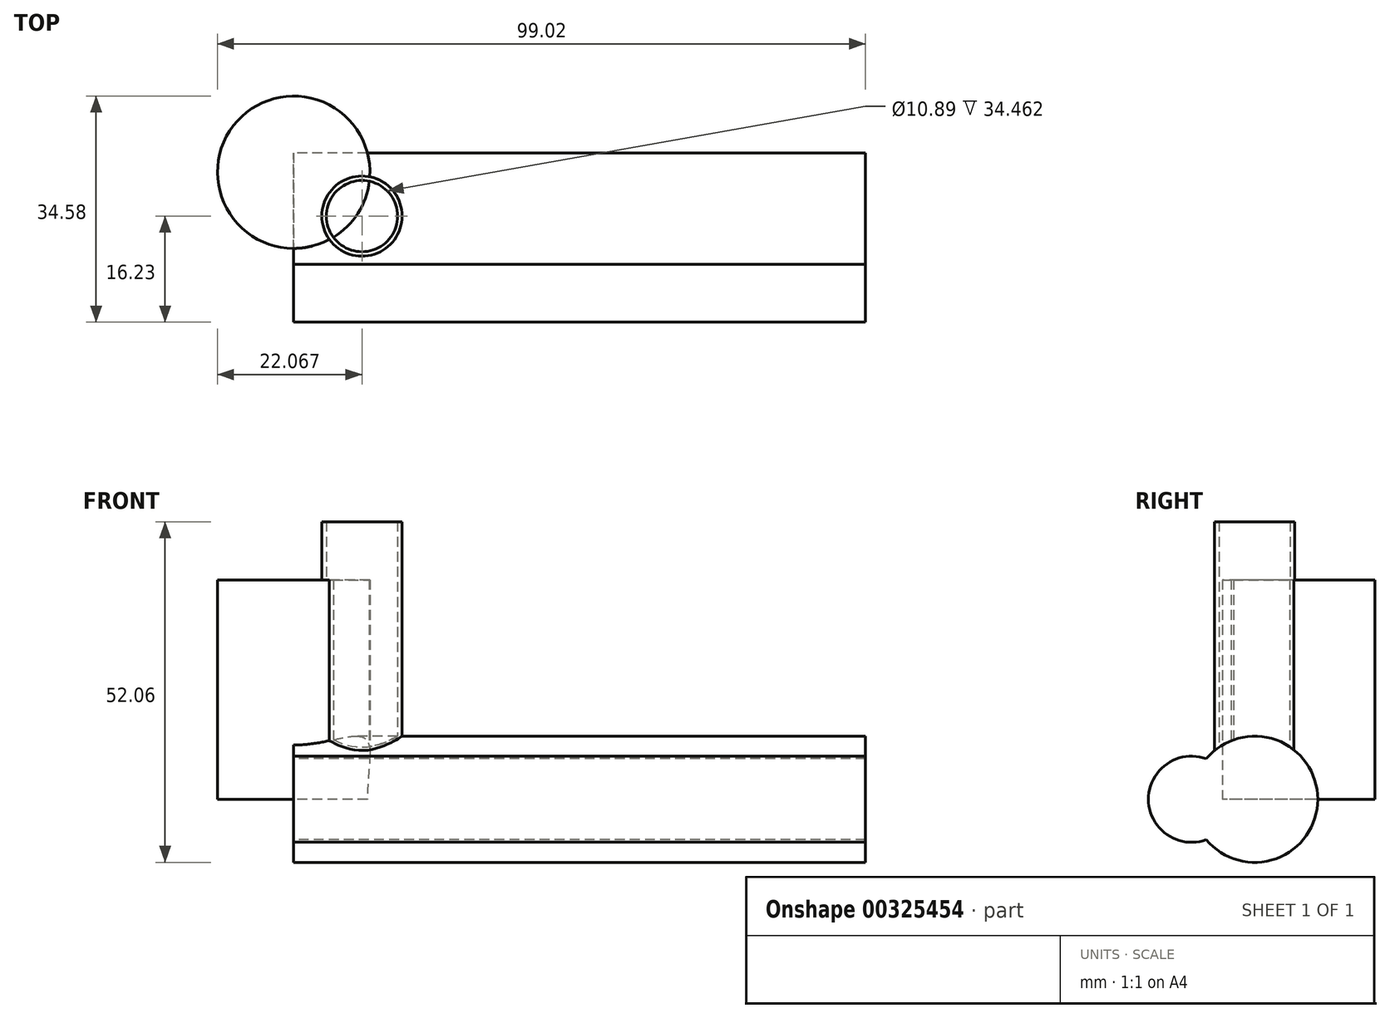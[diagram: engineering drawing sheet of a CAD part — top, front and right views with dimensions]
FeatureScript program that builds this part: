
annotation { "Feature Type Name" : "Feature", "Feature Type Description" : "" }
export const myFeature = defineFeature(function(context is Context, id is Id, definition is map)
    precondition{}
    {
        {
            var Q0;
            Q0=qCreatedBy(makeId("Right.planeOp"),FACE);
            var sketch = newSketch(context, id + "F0", { "sketchPlane" : qUnion([Q0])});
            skCircle(sketch, "E0", {"center": v(0, 0) * mm, "radius": 9.64 * mm});
            skCircle(sketch, "E1", {"center": v(-9.64, 0) * mm, "radius": 6.58 * mm});
            skSolve(sketch);
        }
        {
            var Q0;
            Q0 = qSketchRegion(id + "F0", true);
            extrude(context, id + "F1", {"entities" : qUnion([Q0]), "depth" : 36.58 * mm});
        }
        {
            var Q0;
            Q0=qCreatedBy(makeId("Top.planeOp"),FACE);
            var sketch = newSketch(context, id + "F2", { "sketchPlane" : qUnion([Q0])});
            skCircle(sketch, "E2", {"center": v(10.43, 0) * mm, "radius": 6.13 * mm});
            skCircle(sketch, "E3", {"center": v(10.43, 0) * mm, "radius": 5.44 * mm});
            skSolve(sketch);
        }
        {
            var Q0;
            Q0 = qSketchRegion(id + "F2", true);
            extrude(context, id + "F3", {"entities" : qUnion([Q0]), "operationType" : NewBodyOperationType.ADD, "depth" : 42.42 * mm});
        }
        {
            var Q0;
            Q0=makeQuery(id+"F1.opExtrude","CAP_FACE",FACE,{"disambiguationData":[OSD([sQuery(id+"F0.wireOp",EDGE,"E0"),sQuery(id+"F0.wireOp",EDGE,"E1")])],"isStart":false});
            extrude(context, id + "F4", {"entities" : qUnion([Q0]), "operationType" : NewBodyOperationType.ADD, "depth" : 25.4 * mm});
        }
        {
            var Q0;
            Q0=makeQuery(id+"F4.opExtrude","CAP_FACE",FACE,{"disambiguationData":[OSD([sQuery(id+"F0.wireOp",EDGE,"E0"),sQuery(id+"F0.wireOp",EDGE,"E1")])],"isStart":false});
            extrude(context, id + "F5", {"entities" : qUnion([Q0]), "operationType" : NewBodyOperationType.ADD, "depth" : 25.4 * mm});
        }
        {
            var Q0;
            Q0=qCreatedBy(makeId("Top.planeOp"),FACE);
            var sketch = newSketch(context, id + "F6", { "sketchPlane" : qUnion([Q0])});
            skCircle(sketch, "E4", {"center": v(0, 6.7) * mm, "radius": 11.64 * mm});
            skSolve(sketch);
        }
        {
            var Q0;
            Q0 = qSketchRegion(id + "F6", true);
            extrude(context, id + "F7", {"entities" : qUnion([Q0]), "operationType" : NewBodyOperationType.ADD, "depth" : 33.53 * mm});
        }
    });
